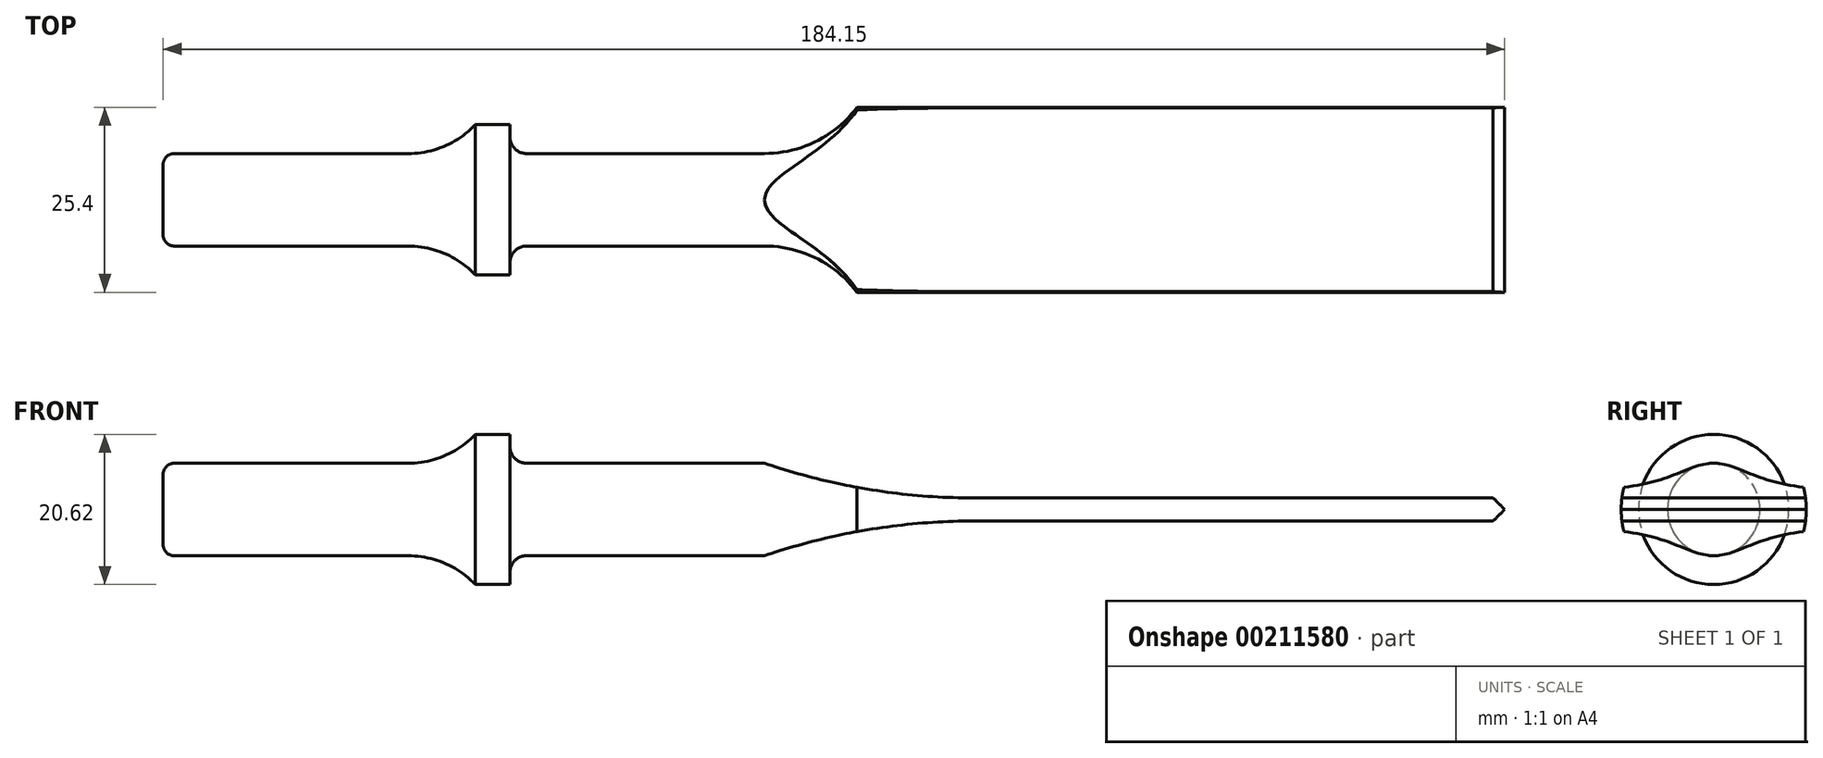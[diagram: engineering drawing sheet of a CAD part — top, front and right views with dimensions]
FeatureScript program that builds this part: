
annotation { "Feature Type Name" : "Feature", "Feature Type Description" : "" }
export const myFeature = defineFeature(function(context is Context, id is Id, definition is map)
    precondition{}
    {
        {
            var Q0;
            Q0=qCreatedBy(makeId("Front.planeOp"),FACE);
            var sketch = newSketch(context, id + "F0", { "sketchPlane" : qUnion([Q0])});
            skLineSegment(sketch, "E0", {"start": v(0, 0) * mm, "end": v(0, 4.83) * mm});
            skLineSegment(sketch, "E1", {"start": v(1.52, 6.35) * mm, "end": v(33.63, 6.35) * mm});
            skLineSegment(sketch, "E2", {"start": v(42.85, 10.31) * mm, "end": v(47.6, 10.31) * mm});
            skLineSegment(sketch, "E3", {"start": v(47.6, 10.31) * mm, "end": v(47.6, 8.64) * mm});
            skPoint(sketch, "E4.visualSharp", {"position": v(0, 6.35) * mm});
            skArc(sketch, "E4.filletArc", {"start": v(1.52, 6.35) * mm, "mid": v(0.45, 5.9) * mm, "end": v(0, 4.83) * mm});
            skLineSegment(sketch, "E5", {"start": v(0, 0) * mm, "end": v(184.15, 0) * mm});
            skLineSegment(sketch, "E6", {"start": v(184.15, 0) * mm, "end": v(184.15, 12.7) * mm});
            skLineSegment(sketch, "E7.0", {"start": v(95.25, 0) * mm, "end": v(95.25, 26.57) * mm, "construction": true});
            skLineSegment(sketch, "E8", {"start": v(184.15, 12.7) * mm, "end": v(95.25, 12.7) * mm});
            skArc(sketch, "E9", {"start": v(82.55, 6.35) * mm, "mid": v(89.65, 8.03) * mm, "end": v(95.25, 12.7) * mm});
            skPoint(sketch, "E9.third.point", {"position": v(66.7, 21.46) * mm});
            skLineSegment(sketch, "E10", {"start": v(82.55, 6.35) * mm, "end": v(49.89, 6.35) * mm});
            skPoint(sketch, "E11.orphan", {"position": v(47.6, 0) * mm});
            skPoint(sketch, "E12.visualSharp", {"position": v(47.6, 6.35) * mm});
            skArc(sketch, "E12.filletArc", {"start": v(47.6, 8.64) * mm, "mid": v(48.27, 7.02) * mm, "end": v(49.89, 6.35) * mm});
            skArc(sketch, "E13", {"start": v(33.63, 6.35) * mm, "mid": v(38.65, 7.38) * mm, "end": v(42.85, 10.31) * mm});
            skPoint(sketch, "E14", {"position": v(42.85, 10.31) * mm});
            skPoint(sketch, "E15.start.orphan", {"position": v(42.85, 6.35) * mm});
            skSolve(sketch);
        }
        {
            var Q0;
            Q0=makeQuery(id+"F0.imprint","IMPRINT",FACE,{"disambiguationData":[TD([[makeQuery(id+"F0.imprint","IMPRINT",EDGE,{"derivedFrom":sQuery(id+"F0.wireOp",EDGE,"E0")}),-1.0]])]});
            var Q1;
            Q1=sQuery(id+"F0.wireOp",EDGE,"E5");
            revolve(context, id + "F1", {"entities" : qUnion([Q0]), "axis" : qUnion([Q1]), "revolveType" : RevolveType.FULL});
        }
        {
            var Q0;
            Q0=qCreatedBy(makeId("Front.planeOp"),FACE);
            var sketch = newSketch(context, id + "F2", { "sketchPlane" : qUnion([Q0])});
            skLineSegment(sketch, "E16", {"start": v(0, 0) * mm, "end": v(184.15, 0) * mm, "construction": true});
            skLineSegment(sketch, "E17.0", {"start": v(0, 1.59) * mm, "end": v(184.15, 1.59) * mm, "construction": true});
            skLineSegment(sketch, "E18", {"start": v(184.15, 0) * mm, "end": v(184.15, 26.1) * mm, "construction": true});
            skLineSegment(sketch, "E19.0", {"start": v(95.25, 0) * mm, "end": v(95.25, 26.1) * mm, "construction": true});
            skLineSegment(sketch, "E20.0", {"start": v(82.55, 0) * mm, "end": v(82.55, 26.1) * mm, "construction": true});
            skLineSegment(sketch, "E21.0", {"start": v(0, 6.35) * mm, "end": v(184.15, 6.35) * mm, "construction": true});
            skArc(sketch, "E22", {"start": v(179.81, 147.08) * mm, "mid": v(30.84, 128.38) * mm, "end": v(111.26, 1.59) * mm});
            skPoint(sketch, "E23", {"position": v(111.26, 1.59) * mm});
            skPoint(sketch, "E24", {"position": v(82.55, 6.35) * mm});
            skLineSegment(sketch, "E25", {"start": v(111.26, 1.59) * mm, "end": v(299.93, 1.59) * mm});
            skLineSegment(sketch, "E26", {"start": v(299.93, 1.59) * mm, "end": v(179.81, 147.08) * mm});
            skLineSegment(sketch, "E27.MirrorCS", {"start": v(111.26, -1.59) * mm, "end": v(299.93, -1.59) * mm});
            skArc(sketch, "E28.MirrorCS", {"start": v(179.81, -147.08) * mm, "mid": v(30.84, -128.38) * mm, "end": v(111.26, -1.59) * mm});
            skLineSegment(sketch, "E29.MirrorCS", {"start": v(299.93, -1.59) * mm, "end": v(179.81, -147.08) * mm});
            skSolve(sketch);
        }
        {
            var Q0;
            Q0=makeQuery(id+"F2.imprint","IMPRINT",FACE,{"disambiguationData":[TD([[makeQuery(id+"F2.imprint","IMPRINT",EDGE,{"derivedFrom":sQuery(id+"F2.wireOp",EDGE,"E22")}),1.0]])]});
            var Q1;
            Q1=makeQuery(id+"F2.imprint","IMPRINT",FACE,{"disambiguationData":[TD([[makeQuery(id+"F2.imprint","IMPRINT",EDGE,{"derivedFrom":sQuery(id+"F2.wireOp",EDGE,"E27.MirrorCS")}),-1.0]])]});
            extrude(context, id + "F3", {"entities" : qUnion([Q0, Q1]), "operationType" : NewBodyOperationType.REMOVE, "oppositeDirection" : true, "depth" : 25.4 * mm});
        }
        {
            var Q0;
            Q0=makeQuery(id+"F2.imprint","IMPRINT",FACE,{"disambiguationData":[TD([[makeQuery(id+"F2.imprint","IMPRINT",EDGE,{"derivedFrom":sQuery(id+"F2.wireOp",EDGE,"E22")}),1.0]])]});
            var Q1;
            Q1=makeQuery(id+"F2.imprint","IMPRINT",FACE,{"disambiguationData":[TD([[makeQuery(id+"F2.imprint","IMPRINT",EDGE,{"derivedFrom":sQuery(id+"F2.wireOp",EDGE,"E27.MirrorCS")}),-1.0]])]});
            extrude(context, id + "F4", {"entities" : qUnion([Q0, Q1]), "operationType" : NewBodyOperationType.REMOVE, "depth" : 25.4 * mm});
        }
        {
            var Q0;
            Q0=qCreatedBy(makeId("Front.planeOp"),FACE);
            var sketch = newSketch(context, id + "F5", { "sketchPlane" : qUnion([Q0])});
            skLineSegment(sketch, "E30", {"start": v(0, 0) * mm, "end": v(184.15, 0) * mm, "construction": true});
            skLineSegment(sketch, "E31", {"start": v(184.15, 0) * mm, "end": v(184.15, 3.8) * mm});
            skLineSegment(sketch, "E32", {"start": v(184.15, 0) * mm, "end": v(180.62, 3.53) * mm});
            skLineSegment(sketch, "E33", {"start": v(180.62, 3.53) * mm, "end": v(184.15, 3.8) * mm});
            skLineSegment(sketch, "E34.MirrorCS", {"start": v(184.15, 0) * mm, "end": v(180.62, -3.53) * mm});
            skLineSegment(sketch, "E35.MirrorCS", {"start": v(180.62, -3.53) * mm, "end": v(184.15, -3.8) * mm});
            skLineSegment(sketch, "E36.MirrorCS", {"start": v(184.15, 0) * mm, "end": v(184.15, -3.8) * mm});
            skSolve(sketch);
        }
        {
            var Q0;
            Q0=makeQuery(id+"F5.imprint","IMPRINT",FACE,{"disambiguationData":[TD([[makeQuery(id+"F5.imprint","IMPRINT",EDGE,{"derivedFrom":sQuery(id+"F5.wireOp",EDGE,"E34.MirrorCS")}),1.0]])]});
            var Q1;
            Q1=makeQuery(id+"F5.imprint","IMPRINT",FACE,{"disambiguationData":[TD([[makeQuery(id+"F5.imprint","IMPRINT",EDGE,{"derivedFrom":sQuery(id+"F5.wireOp",EDGE,"E31")}),1.0]])]});
            extrude(context, id + "F6", {"entities" : qUnion([Q0, Q1]), "operationType" : NewBodyOperationType.REMOVE, "oppositeDirection" : true, "depth" : 25.4 * mm});
        }
        {
            var Q0;
            Q0 = qSketchRegion(id + "F5", true);
            extrude(context, id + "F7", {"entities" : qUnion([Q0]), "operationType" : NewBodyOperationType.REMOVE, "depth" : 25.4 * mm});
        }
    });
